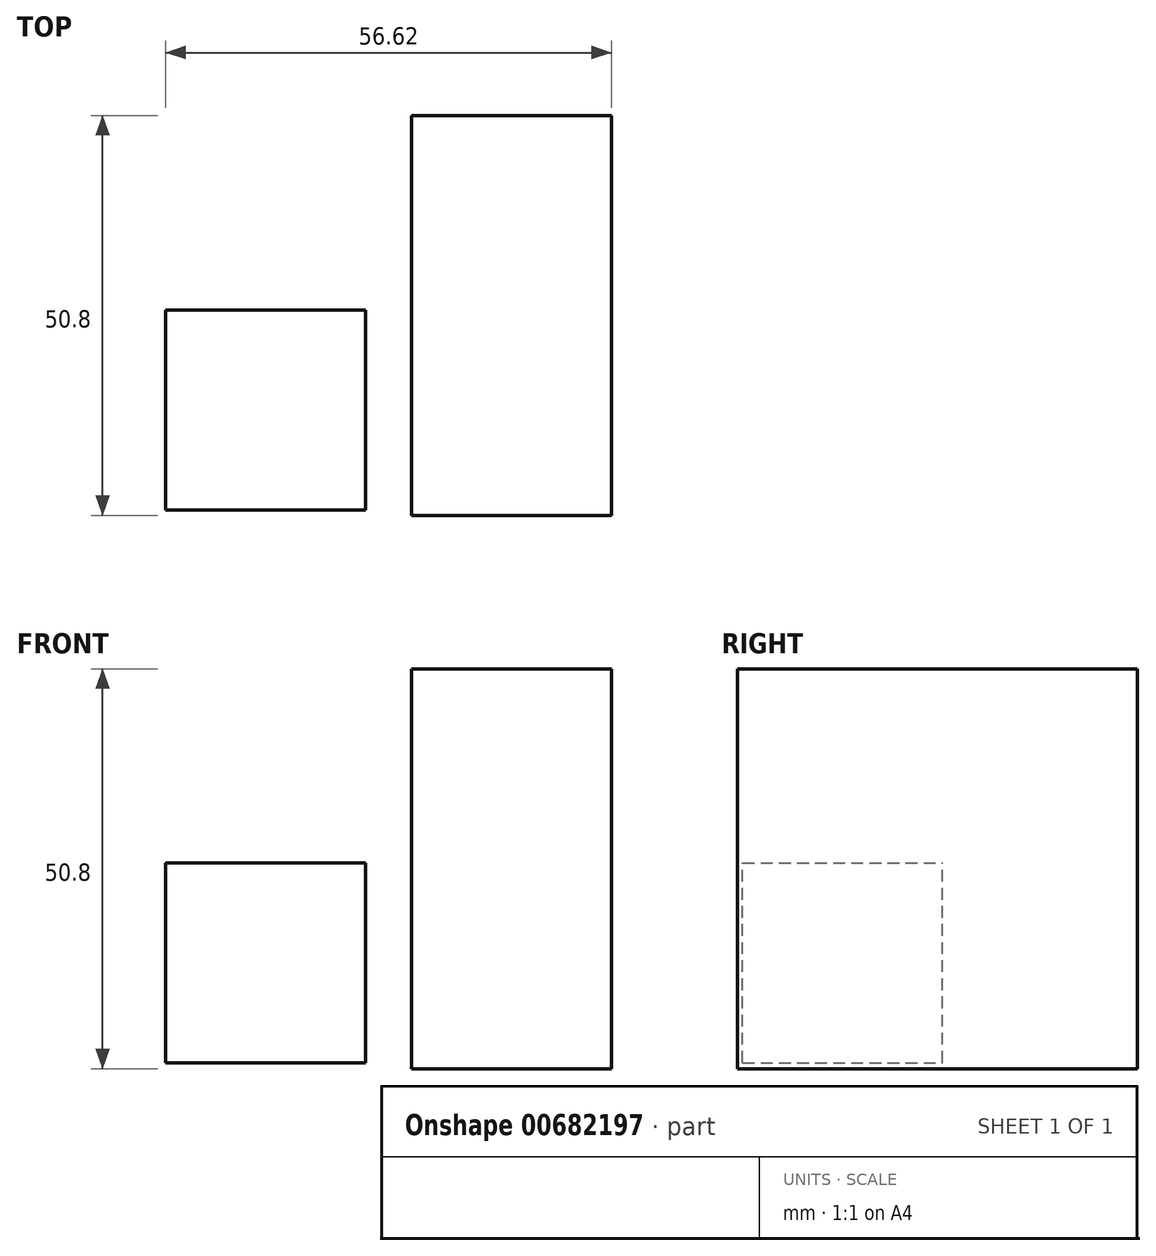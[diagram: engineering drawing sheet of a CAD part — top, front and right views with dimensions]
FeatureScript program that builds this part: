
annotation { "Feature Type Name" : "Feature", "Feature Type Description" : "" }
export const myFeature = defineFeature(function(context is Context, id is Id, definition is map)
    precondition{}
    {
        {
            var Q0;
            Q0=qCreatedBy(makeId("Front.planeOp"),FACE);
            var sketch = newSketch(context, id + "F0", { "sketchPlane" : qUnion([Q0])});
            skLineSegment(sketch, "E0.bottom", {"start": v(31.22, 19.58) * mm, "end": v(56.62, 19.58) * mm});
            skLineSegment(sketch, "E0.top", {"start": v(31.22, -31.22) * mm, "end": v(56.62, -31.22) * mm});
            skLineSegment(sketch, "E0.left", {"start": v(31.22, 19.58) * mm, "end": v(31.22, -31.22) * mm});
            skLineSegment(sketch, "E0.right", {"start": v(56.62, 19.58) * mm, "end": v(56.62, -31.22) * mm});
            skSolve(sketch);
        }
        {
            var Q0;
            Q0 = qSketchRegion(id + "F0", true);
            extrude(context, id + "F1", {"entities" : qUnion([Q0]), "depth" : 50.8 * mm, "offsetDistance" : 25.4 * mm});
        }
        {
            var Q0;
            Q0=qCreatedBy(makeId("Right.planeOp"),FACE);
            var sketch = newSketch(context, id + "F2", { "sketchPlane" : qUnion([Q0])});
            skLineSegment(sketch, "E1.bottom", {"start": v(-50.13, -30.46) * mm, "end": v(-24.73, -30.46) * mm});
            skLineSegment(sketch, "E1.top", {"start": v(-50.13, -5.06) * mm, "end": v(-24.73, -5.06) * mm});
            skLineSegment(sketch, "E1.left", {"start": v(-50.13, -30.46) * mm, "end": v(-50.13, -5.06) * mm});
            skLineSegment(sketch, "E1.right", {"start": v(-24.73, -30.46) * mm, "end": v(-24.73, -5.06) * mm});
            skSolve(sketch);
        }
        {
            var Q0;
            Q0 = qSketchRegion(id + "F2", true);
            extrude(context, id + "F3", {"entities" : qUnion([Q0]), "depth" : 25.4 * mm, "offsetDistance" : 25.4 * mm});
        }
    });
